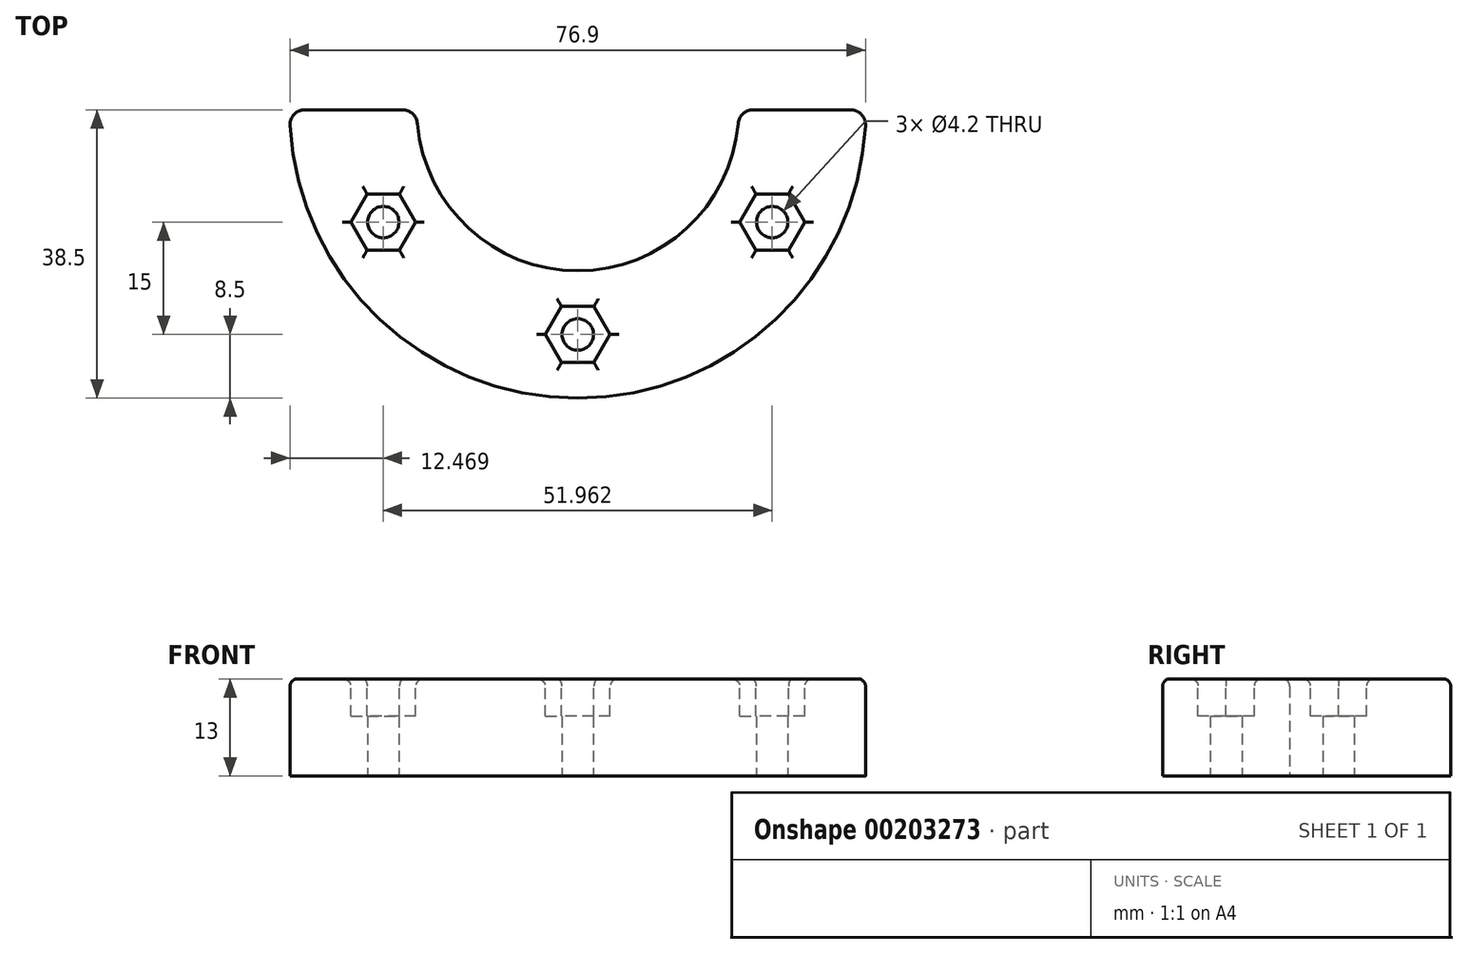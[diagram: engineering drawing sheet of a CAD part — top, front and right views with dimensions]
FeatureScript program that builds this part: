
annotation { "Feature Type Name" : "Feature", "Feature Type Description" : "" }
export const myFeature = defineFeature(function(context is Context, id is Id, definition is map)
    precondition{}
    {
        {
            var Q0;
            Q0=qCreatedBy(makeId("Top.planeOp"),FACE);
            var sketch = newSketch(context, id + "F0", { "sketchPlane" : qUnion([Q0])});
            skArc(sketch, "E0", {"start": v(-21.42, -1.83) * mm, "mid": v(0, -21.5) * mm, "end": v(21.42, -1.83) * mm});
            skArc(sketch, "E1", {"start": v(-38.44, -2.1) * mm, "mid": v(0, -38.5) * mm, "end": v(38.44, -2.1) * mm});
            skLineSegment(sketch, "E2", {"start": v(-23.41, 0) * mm, "end": v(-36.45, 0) * mm});
            skLineSegment(sketch, "E3", {"start": v(23.41, 0) * mm, "end": v(36.45, 0) * mm});
            skPoint(sketch, "E4.visualSharp", {"position": v(-38.5, 0) * mm});
            skArc(sketch, "E4.filletArc", {"start": v(-36.45, 0) * mm, "mid": v(-37.9, -0.63) * mm, "end": v(-38.44, -2.1) * mm});
            skPoint(sketch, "E5.visualSharp", {"position": v(-21.5, 0) * mm});
            skArc(sketch, "E5.filletArc", {"start": v(-21.42, -1.83) * mm, "mid": v(-22.06, -0.53) * mm, "end": v(-23.41, 0) * mm});
            skPoint(sketch, "E6.visualSharp", {"position": v(21.5, 0) * mm});
            skArc(sketch, "E6.filletArc", {"start": v(23.41, 0) * mm, "mid": v(22.06, -0.53) * mm, "end": v(21.42, -1.83) * mm});
            skPoint(sketch, "E7.visualSharp", {"position": v(38.5, 0) * mm});
            skArc(sketch, "E7.filletArc", {"start": v(38.44, -2.1) * mm, "mid": v(37.9, -0.63) * mm, "end": v(36.45, 0) * mm});
            skSolve(sketch);
        }
        {
            var Q0;
            Q0 = qSketchRegion(id + "F0", true);
            extrude(context, id + "F1", {"entities" : qUnion([Q0]), "depth" : 13 * mm});
        }
        {
            var Q0;
            Q0=makeQuery(id+"F0.imprint","IMPRINT",FACE,{"disambiguationData":[TD([[makeQuery(id+"F0.imprint","IMPRINT",EDGE,{"derivedFrom":sQuery(id+"F0.wireOp",EDGE,"E0")}),-1.0]])]});
            var sketch = newSketch(context, id + "F2", { "sketchPlane" : qUnion([Q0])});
            skCircle(sketch, "E8", {"center": v(-25.98, -15) * mm, "radius": 2.1 * mm});
            skCircle(sketch, "E9", {"center": v(0, -30) * mm, "radius": 2.1 * mm});
            skCircle(sketch, "E10", {"center": v(25.98, -15) * mm, "radius": 2.1 * mm});
            skArc(sketch, "E11", {"start": v(-25.98, -15) * mm, "mid": v(0, -30) * mm, "end": v(25.98, -15) * mm, "construction": true});
            skLineSegment(sketch, "E12", {"start": v(0, 0) * mm, "end": v(-25.98, -15) * mm, "construction": true});
            skLineSegment(sketch, "E13", {"start": v(0, 0) * mm, "end": v(25.98, -15) * mm, "construction": true});
            skLineSegment(sketch, "E14", {"start": v(0, 0) * mm, "end": v(0, -30) * mm, "construction": true});
            skSolve(sketch);
        }
        {
            var Q0;
            Q0 = qSketchRegion(id + "F2", true);
            extrude(context, id + "F3", {"entities" : qUnion([Q0]), "operationType" : NewBodyOperationType.REMOVE, "endBound" : BoundingType.THROUGH_ALL, "depth" : 25 * mm});
        }
        {
            var Q0;
            Q0=makeQuery(id+"F1.opExtrude","CAP_FACE",FACE,{"disambiguationData":[OSD([sQuery(id+"F0.wireOp",EDGE,"E0"),sQuery(id+"F0.wireOp",EDGE,"EQFJpnYF-5bmR-9Rxz-qQCj-KMBcESOZMTfp.bottom"),sQuery(id+"F0.wireOp",EDGE,"EQFJpnYF-5bmR-9Rxz-qQCj-KMBcESOZMTfp.top"),sQuery(id+"F0.wireOp",EDGE,"EQFJpnYF-5bmR-9Rxz-qQCj-KMBcESOZMTfp.left"),sQuery(id+"F0.wireOp",EDGE,"EQFJpnYF-5bmR-9Rxz-qQCj-KMBcESOZMTfp.right"),sQuery(id+"F0.wireOp",EDGE,"167afbe8-75fa-4542-9c05-f5845217e859.trimOffspring")])],"isStart":false});
            var sketch = newSketch(context, id + "F4", { "sketchPlane" : qUnion([Q0])});
            skCircle(sketch, "E15.cCircle", {"center": v(-25.98, -15) * mm, "radius": 3.75 * mm, "construction": true});
            skLineSegment(sketch, "E15.0", {"start": v(-21.65, -15) * mm, "end": v(-23.82, -18.75) * mm});
            skLineSegment(sketch, "E15.1", {"start": v(-23.82, -18.75) * mm, "end": v(-28.15, -18.75) * mm});
            skLineSegment(sketch, "E15.2", {"start": v(-28.15, -18.75) * mm, "end": v(-30.31, -15) * mm});
            skLineSegment(sketch, "E15.3", {"start": v(-30.31, -15) * mm, "end": v(-28.15, -11.25) * mm});
            skLineSegment(sketch, "E15.4", {"start": v(-28.15, -11.25) * mm, "end": v(-23.82, -11.25) * mm});
            skLineSegment(sketch, "E15.5", {"start": v(-23.82, -11.25) * mm, "end": v(-21.65, -15) * mm});
            skPoint(sketch, "E15.0.midPoint", {"position": v(-22.73, -16.88) * mm});
            skCircle(sketch, "E16.cCircle", {"center": v(0, -30) * mm, "radius": 3.75 * mm, "construction": true});
            skLineSegment(sketch, "E16.0", {"start": v(2.17, -33.75) * mm, "end": v(-2.17, -33.75) * mm});
            skLineSegment(sketch, "E16.1", {"start": v(-2.17, -33.75) * mm, "end": v(-4.33, -30) * mm});
            skLineSegment(sketch, "E16.2", {"start": v(-4.33, -30) * mm, "end": v(-2.17, -26.25) * mm});
            skLineSegment(sketch, "E16.3", {"start": v(-2.17, -26.25) * mm, "end": v(2.17, -26.25) * mm});
            skLineSegment(sketch, "E16.4", {"start": v(2.17, -26.25) * mm, "end": v(4.33, -30) * mm});
            skLineSegment(sketch, "E16.5", {"start": v(4.33, -30) * mm, "end": v(2.17, -33.75) * mm});
            skPoint(sketch, "E16.0.midPoint", {"position": v(0, -33.75) * mm});
            skCircle(sketch, "E17.cCircle", {"center": v(25.98, -15) * mm, "radius": 3.75 * mm, "construction": true});
            skLineSegment(sketch, "E17.0", {"start": v(28.15, -18.75) * mm, "end": v(23.82, -18.75) * mm});
            skLineSegment(sketch, "E17.1", {"start": v(23.82, -18.75) * mm, "end": v(21.65, -15) * mm});
            skLineSegment(sketch, "E17.2", {"start": v(21.65, -15) * mm, "end": v(23.82, -11.25) * mm});
            skLineSegment(sketch, "E17.3", {"start": v(23.82, -11.25) * mm, "end": v(28.15, -11.25) * mm});
            skLineSegment(sketch, "E17.4", {"start": v(28.15, -11.25) * mm, "end": v(30.31, -15) * mm});
            skLineSegment(sketch, "E17.5", {"start": v(30.31, -15) * mm, "end": v(28.15, -18.75) * mm});
            skPoint(sketch, "E17.0.midPoint", {"position": v(25.98, -18.75) * mm});
            skSolve(sketch);
        }
        {
            var Q0;
            Q0 = qSketchRegion(id + "F4", true);
            extrude(context, id + "F5", {"entities" : qUnion([Q0]), "operationType" : NewBodyOperationType.REMOVE, "oppositeDirection" : true, "depth" : 5 * mm});
        }
        {
            var Q0;
            Q0=makeQuery(id+"F1.opExtrude","CAP_FACE",FACE,{"disambiguationData":[OSD([sQuery(id+"F0.wireOp",EDGE,"E0"),sQuery(id+"F0.wireOp",EDGE,"E1"),sQuery(id+"F0.wireOp",EDGE,"E2"),sQuery(id+"F0.wireOp",EDGE,"E3"),sQuery(id+"F0.wireOp",EDGE,"E4.filletArc"),sQuery(id+"F0.wireOp",EDGE,"E5.filletArc"),sQuery(id+"F0.wireOp",EDGE,"E6.filletArc"),sQuery(id+"F0.wireOp",EDGE,"E7.filletArc")])],"isStart":false});
            fillet(context, id + "F6", {"entities" : qUnion([Q0]), "radius" : 1 * mm, "tangentPropagation" : true, "allowEdgeOverflow" : false});
        }
    });
